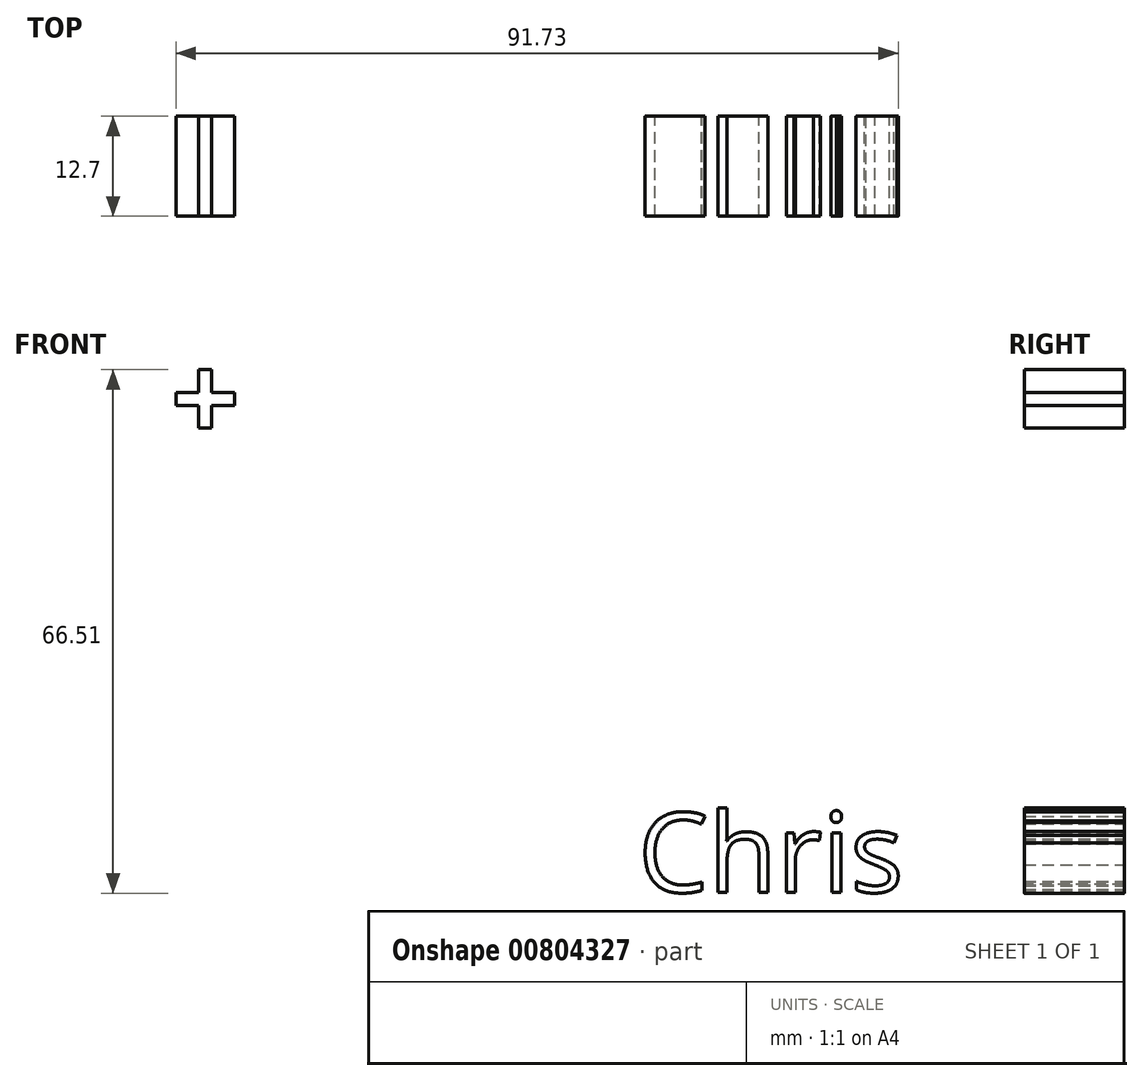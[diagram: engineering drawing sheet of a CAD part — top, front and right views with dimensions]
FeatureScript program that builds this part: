
annotation { "Feature Type Name" : "Feature", "Feature Type Description" : "" }
export const myFeature = defineFeature(function(context is Context, id is Id, definition is map)
    precondition{}
    {
        {
            var Q0;
            Q0=qCreatedBy(makeId("Front.planeOp"),FACE);
            var sketch = newSketch(context, id + "F0", { "sketchPlane" : qUnion([Q0])});
            skText(sketch, "E0", { "text": "Chris", "fontName": "OpenSans-Regular.ttf"});
            const initialGuessF0  = {"E0": [-0.0162, 0, 1, 0, 0.01017]};
            skSetInitialGuess(sketch, initialGuessF0);
            skSolve(sketch);
        }
        {
            var Q0;
            Q0 = qSketchRegion(id + "F0", true);
            extrude(context, id + "F1", {"entities" : qUnion([Q0]), "depth" : 12.7 * mm, "offsetDistance" : 25.4 * mm});
        }
        {
            var Q0;
            Q0=qCreatedBy(makeId("Front.planeOp"),FACE);
            var sketch = newSketch(context, id + "F2", { "sketchPlane" : qUnion([Q0])});
            skText(sketch, "E1", { "text": "+", "fontName": "OpenSans-Bold.ttf"});
            const initialGuessF2  = {"E1": [-0.07558, 0.05726, 1, 0, 0.011]};
            skSetInitialGuess(sketch, initialGuessF2);
            skSolve(sketch);
        }
        {
            var Q0;
            Q0 = qSketchRegion(id + "F2", true);
            extrude(context, id + "F3", {"entities" : qUnion([Q0]), "depth" : 12.7 * mm, "offsetDistance" : 25.4 * mm});
        }
    });
